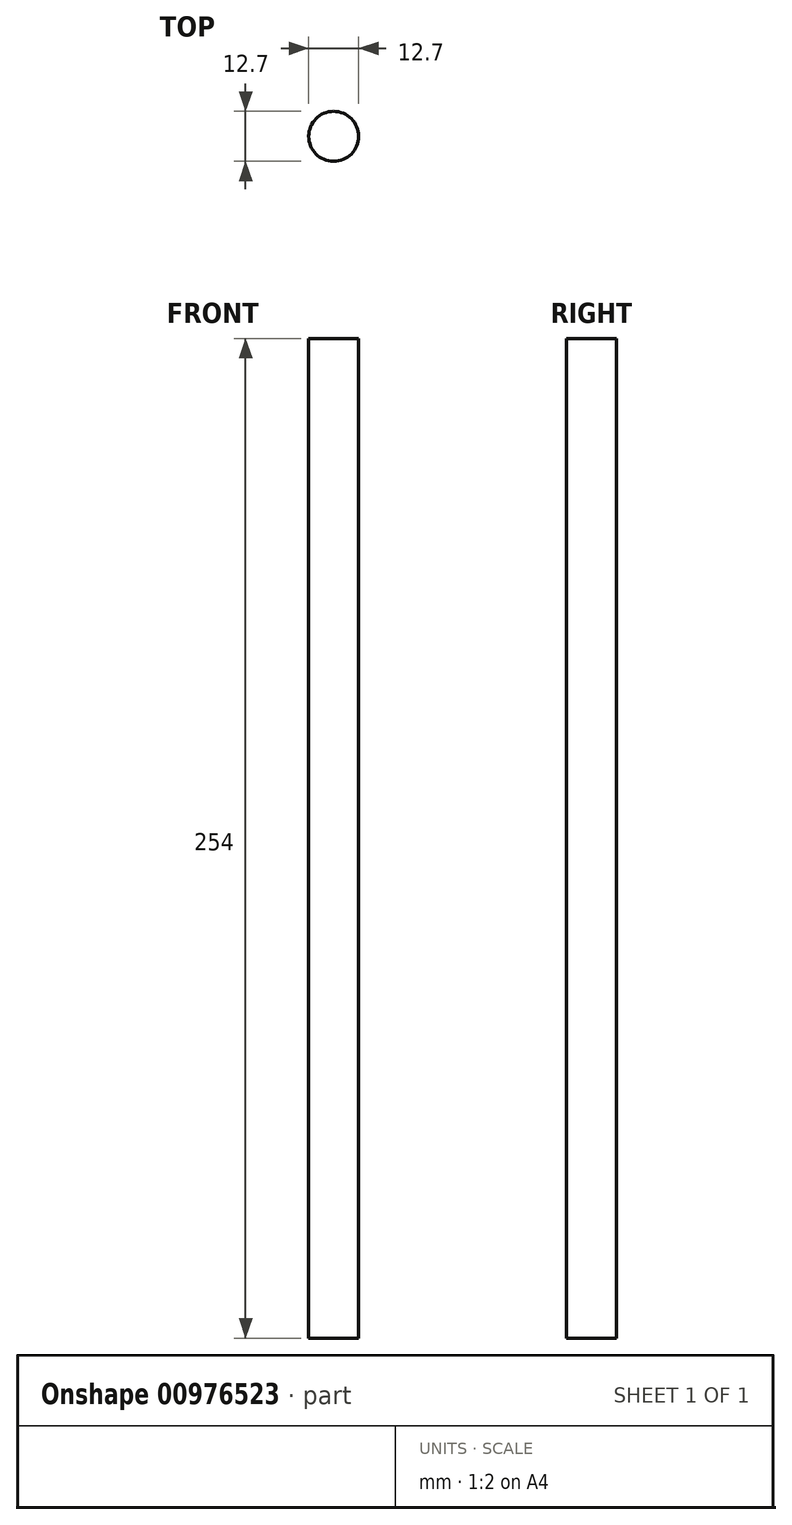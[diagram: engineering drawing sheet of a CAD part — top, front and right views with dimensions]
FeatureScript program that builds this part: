
annotation { "Feature Type Name" : "Feature", "Feature Type Description" : "" }
export const myFeature = defineFeature(function(context is Context, id is Id, definition is map)
    precondition{}
    {
        {
            var Q0;
            Q0=qCreatedBy(makeId("Top.planeOp"),FACE);
            var sketch = newSketch(context, id + "F0", { "sketchPlane" : qUnion([Q0])});
            skCircle(sketch, "E0", {"center": v(-33.33, 73.2) * mm, "radius": 6.35 * mm});
            skSolve(sketch);
        }
        {
            var Q0;
            Q0=makeQuery(id+"F0.imprint","IMPRINT",FACE,{"disambiguationData":[TD([[makeQuery(id+"F0.imprint","IMPRINT",EDGE,{"derivedFrom":sQuery(id+"F0.wireOp",EDGE,"E0")}),1.0]])]});
            extrude(context, id + "F1", {"entities" : qUnion([Q0]), "depth" : 254 * mm, "offsetDistance" : 25.4 * mm});
        }
    });
